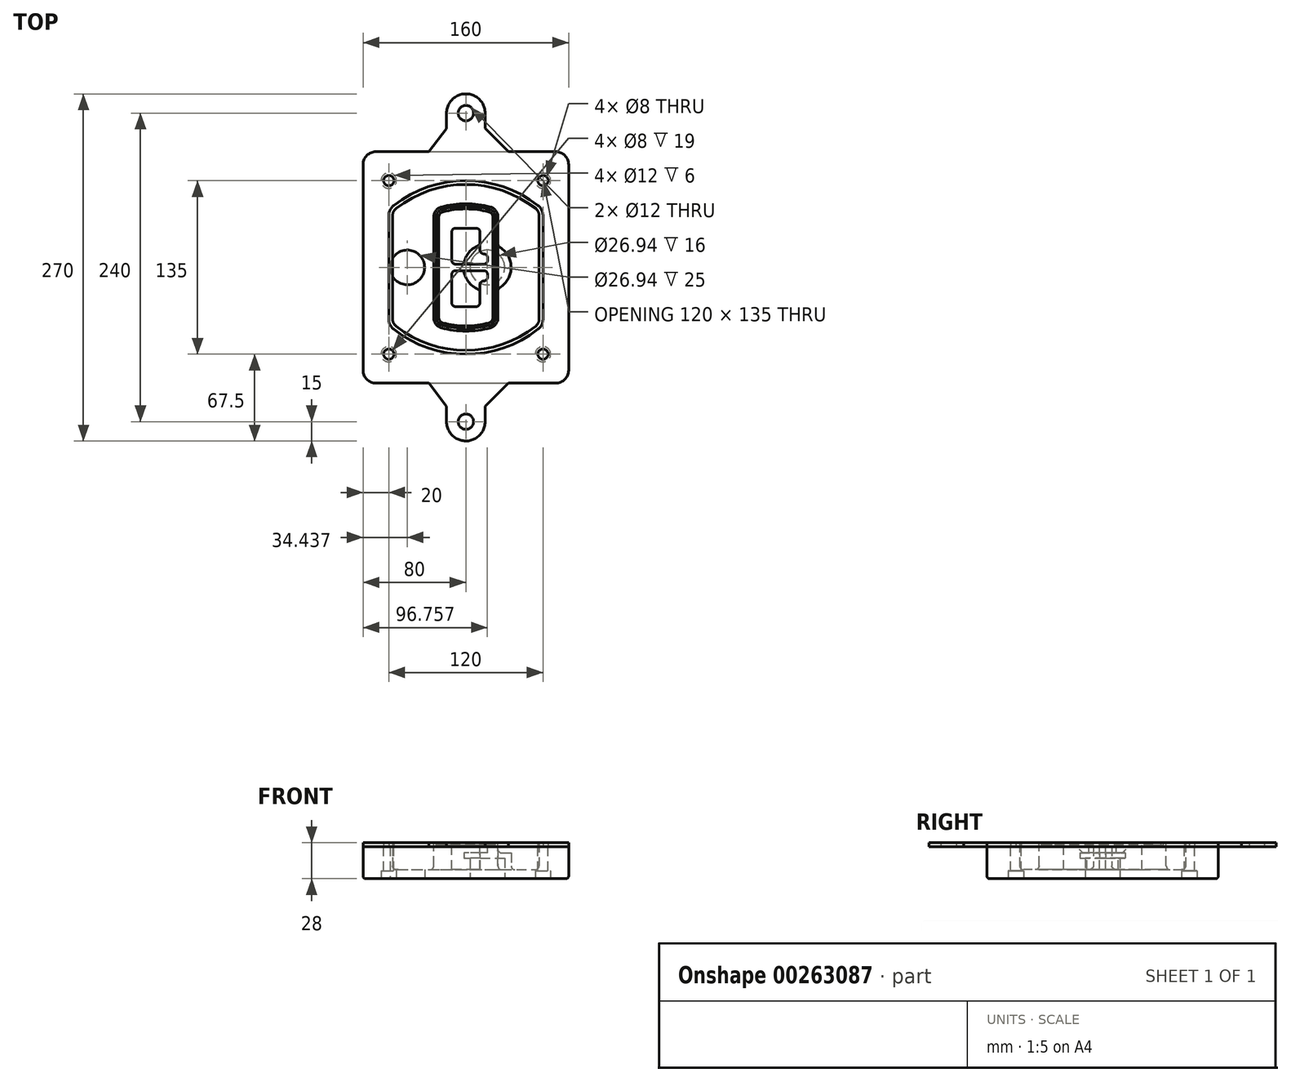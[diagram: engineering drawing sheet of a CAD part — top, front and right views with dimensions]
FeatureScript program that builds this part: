
annotation { "Feature Type Name" : "Feature", "Feature Type Description" : "" }
export const myFeature = defineFeature(function(context is Context, id is Id, definition is map)
    precondition{}
    {
        {
            var Q0;
            Q0=qCreatedBy(makeId("Top.planeOp"),FACE);
            var sketch = newSketch(context, id + "F0", { "sketchPlane" : qUnion([Q0])});
            skPoint(sketch, "E0.rect.middle", {"position": v(0, 0) * mm});
            skLineSegment(sketch, "E1.bottom", {"start": v(-70, -90) * mm, "end": v(70, -90) * mm});
            skLineSegment(sketch, "E1.top", {"start": v(-70, 90) * mm, "end": v(70, 90) * mm});
            skLineSegment(sketch, "E1.left", {"start": v(-80, -80) * mm, "end": v(-80, 80) * mm});
            skLineSegment(sketch, "E1.right", {"start": v(80, -80) * mm, "end": v(80, 80) * mm});
            skLineSegment(sketch, "E2", {"start": v(-80, 90) * mm, "end": v(80, -90) * mm, "construction": true});
            skLineSegment(sketch, "E3", {"start": v(80, 90) * mm, "end": v(-80, -90) * mm, "construction": true});
            skCircle(sketch, "E4", {"center": v(-60, 67.5) * mm, "radius": 4 * mm});
            skCircle(sketch, "E5", {"center": v(60, 67.5) * mm, "radius": 4 * mm});
            skCircle(sketch, "E6", {"center": v(60, -67.5) * mm, "radius": 4 * mm});
            skCircle(sketch, "E7", {"center": v(-60, -67.5) * mm, "radius": 4 * mm});
            skLineSegment(sketch, "E8", {"start": v(-60, 67.5) * mm, "end": v(60, 67.5) * mm, "construction": true});
            skLineSegment(sketch, "E9", {"start": v(60, 67.5) * mm, "end": v(60, -67.5) * mm, "construction": true});
            skLineSegment(sketch, "E10", {"start": v(60, -67.5) * mm, "end": v(-60, -67.5) * mm, "construction": true});
            skLineSegment(sketch, "E11", {"start": v(-60, -67.5) * mm, "end": v(-60, 67.5) * mm, "construction": true});
            skLineSegment(sketch, "E12", {"start": v(-60, 40.3) * mm, "end": v(-60, -40.3) * mm});
            skLineSegment(sketch, "E13", {"start": v(60, 40.3) * mm, "end": v(60, -40.3) * mm});
            skArc(sketch, "E14", {"start": v(56.15, 48.18) * mm, "mid": v(0, 67.5) * mm, "end": v(-56.15, 48.18) * mm});
            skArc(sketch, "E15", {"start": v(-56.15, -48.18) * mm, "mid": v(0, -67.5) * mm, "end": v(56.15, -48.18) * mm});
            skLineSegment(sketch, "E16", {"start": v(-60, 0) * mm, "end": v(60, 0) * mm, "construction": true});
            skPoint(sketch, "E17.visualSharp", {"position": v(-60, -45) * mm});
            skArc(sketch, "E17.filletArc", {"start": v(-60, -40.3) * mm, "mid": v(-58.99, -44.68) * mm, "end": v(-56.15, -48.18) * mm});
            skPoint(sketch, "E18.visualSharp", {"position": v(-60, 45) * mm});
            skArc(sketch, "E18.filletArc", {"start": v(-56.15, 48.18) * mm, "mid": v(-58.99, 44.68) * mm, "end": v(-60, 40.3) * mm});
            skPoint(sketch, "E19.visualSharp", {"position": v(60, 45) * mm});
            skArc(sketch, "E19.filletArc", {"start": v(60, 40.3) * mm, "mid": v(58.99, 44.68) * mm, "end": v(56.15, 48.18) * mm});
            skPoint(sketch, "E20.visualSharp", {"position": v(60, -45) * mm});
            skArc(sketch, "E20.filletArc", {"start": v(56.15, -48.18) * mm, "mid": v(58.99, -44.68) * mm, "end": v(60, -40.3) * mm});
            skPoint(sketch, "E21.visualSharp", {"position": v(-80, 90) * mm});
            skArc(sketch, "E21.filletArc", {"start": v(-70, 90) * mm, "mid": v(-77.07, 87.07) * mm, "end": v(-80, 80) * mm});
            skPoint(sketch, "E22.visualSharp", {"position": v(80, 90) * mm});
            skArc(sketch, "E22.filletArc", {"start": v(80, 80) * mm, "mid": v(77.07, 87.07) * mm, "end": v(70, 90) * mm});
            skPoint(sketch, "E23.visualSharp", {"position": v(80, -90) * mm});
            skArc(sketch, "E23.filletArc", {"start": v(70, -90) * mm, "mid": v(77.07, -87.07) * mm, "end": v(80, -80) * mm});
            skPoint(sketch, "E24.visualSharp", {"position": v(-80, -90) * mm});
            skArc(sketch, "E24.filletArc", {"start": v(-80, -80) * mm, "mid": v(-77.07, -87.07) * mm, "end": v(-70, -90) * mm});
            skArc(sketch, "E25.0", {"start": v(57, 40.3) * mm, "mid": v(56.3, 43.36) * mm, "end": v(54.3, 45.81) * mm});
            skLineSegment(sketch, "E25.1", {"start": v(57, 40.3) * mm, "end": v(57, -40.3) * mm});
            skArc(sketch, "E25.2", {"start": v(54.3, -45.81) * mm, "mid": v(56.3, -43.36) * mm, "end": v(57, -40.3) * mm});
            skArc(sketch, "E25.3", {"start": v(-54.3, -45.81) * mm, "mid": v(0, -64.5) * mm, "end": v(54.3, -45.81) * mm});
            skArc(sketch, "E25.4", {"start": v(-57, -40.3) * mm, "mid": v(-56.3, -43.36) * mm, "end": v(-54.3, -45.81) * mm});
            skArc(sketch, "E25.5", {"start": v(54.3, 45.81) * mm, "mid": v(0, 64.5) * mm, "end": v(-54.3, 45.81) * mm});
            skLineSegment(sketch, "E25.6", {"start": v(-57, 40.3) * mm, "end": v(-57, -40.3) * mm});
            skArc(sketch, "E25.7", {"start": v(-54.3, 45.81) * mm, "mid": v(-56.3, 43.36) * mm, "end": v(-57, 40.3) * mm});
            skArc(sketch, "E26.0", {"start": v(-58.62, 51.33) * mm, "mid": v(-62.58, 46.43) * mm, "end": v(-64, 40.3) * mm});
            skArc(sketch, "E26.1", {"start": v(58.62, 51.33) * mm, "mid": v(0, 71.5) * mm, "end": v(-58.62, 51.33) * mm});
            skArc(sketch, "E26.2", {"start": v(64, 40.3) * mm, "mid": v(62.58, 46.43) * mm, "end": v(58.62, 51.33) * mm});
            skLineSegment(sketch, "E26.3", {"start": v(64, 40.3) * mm, "end": v(64, -40.3) * mm});
            skArc(sketch, "E26.4", {"start": v(58.62, -51.33) * mm, "mid": v(62.58, -46.43) * mm, "end": v(64, -40.3) * mm});
            skLineSegment(sketch, "E26.5", {"start": v(-64, 40.3) * mm, "end": v(-64, -40.3) * mm});
            skArc(sketch, "E26.6", {"start": v(-58.62, -51.33) * mm, "mid": v(0, -71.5) * mm, "end": v(58.62, -51.33) * mm});
            skArc(sketch, "E26.7", {"start": v(-64, -40.3) * mm, "mid": v(-62.58, -46.43) * mm, "end": v(-58.62, -51.33) * mm});
            skSolve(sketch);
        }
        {
            var Q0;
            Q0=makeQuery(id+"F0.imprint","IMPRINT",FACE,{"disambiguationData":[TD([[makeQuery(id+"F0.imprint","IMPRINT",EDGE,{"derivedFrom":sQuery(id+"F0.wireOp",EDGE,"E1.bottom")}),1.0]])]});
            var Q1;
            Q1=makeQuery(id+"F0.imprint","IMPRINT",FACE,{"disambiguationData":[TD([[makeQuery(id+"F0.imprint","IMPRINT",EDGE,{"derivedFrom":sQuery(id+"F0.wireOp",EDGE,"E12")}),1.0]])]});
            var Q2;
            Q2=makeQuery(id+"F0.imprint","IMPRINT",FACE,{"disambiguationData":[TD([[makeQuery(id+"F0.imprint","IMPRINT",EDGE,{"derivedFrom":sQuery(id+"F0.wireOp",EDGE,"E25.0")}),1.0]])]});
            var Q3;
            Q3=makeQuery(id+"F0.imprint","IMPRINT",FACE,{"disambiguationData":[TD([[makeQuery(id+"F0.imprint","IMPRINT",EDGE,{"derivedFrom":sQuery(id+"F0.wireOp",EDGE,"E12")}),-1.0]])]});
            extrude(context, id + "F1", {"entities" : qUnion([Q0, Q1, Q2, Q3]), "oppositeDirection" : true, "depth" : 25 * mm});
        }
        {
            var Q0;
            Q0=makeQuery(id+"F0.imprint","IMPRINT",FACE,{"disambiguationData":[TD([[makeQuery(id+"F0.imprint","IMPRINT",EDGE,{"derivedFrom":sQuery(id+"F0.wireOp",EDGE,"E12")}),1.0]])]});
            extrude(context, id + "F2", {"entities" : qUnion([Q0]), "operationType" : NewBodyOperationType.ADD, "depth" : 3 * mm});
        }
        {
            var Q0;
            Q0=makeQuery(id+"F0.imprint","IMPRINT",FACE,{"disambiguationData":[TD([[makeQuery(id+"F0.imprint","IMPRINT",EDGE,{"derivedFrom":sQuery(id+"F0.wireOp",EDGE,"E25.0")}),1.0]])]});
            extrude(context, id + "F3", {"entities" : qUnion([Q0]), "operationType" : NewBodyOperationType.REMOVE, "oppositeDirection" : true, "depth" : 18 * mm});
        }
        {
            var Q0;
            Q0=makeQuery(id+"F2.opExtrude","CAP_FACE",FACE,{"disambiguationData":[OSD([sQuery(id+"F0.wireOp",EDGE,"E12"),sQuery(id+"F0.wireOp",EDGE,"E13"),sQuery(id+"F0.wireOp",EDGE,"E14"),sQuery(id+"F0.wireOp",EDGE,"E15"),sQuery(id+"F0.wireOp",EDGE,"E17.filletArc"),sQuery(id+"F0.wireOp",EDGE,"E18.filletArc"),sQuery(id+"F0.wireOp",EDGE,"E19.filletArc"),sQuery(id+"F0.wireOp",EDGE,"E20.filletArc"),sQuery(id+"F0.wireOp",EDGE,"E25.0"),sQuery(id+"F0.wireOp",EDGE,"E25.1"),sQuery(id+"F0.wireOp",EDGE,"E25.2"),sQuery(id+"F0.wireOp",EDGE,"E25.3"),sQuery(id+"F0.wireOp",EDGE,"E25.4"),sQuery(id+"F0.wireOp",EDGE,"E25.5"),sQuery(id+"F0.wireOp",EDGE,"E25.6"),sQuery(id+"F0.wireOp",EDGE,"E25.7")])],"isStart":false});
            var sketch = newSketch(context, id + "F4", { "sketchPlane" : qUnion([Q0])});
            skArc(sketch, "E27.0", {"start": v(-19.08, -46.97) * mm, "mid": v(0, -49.5) * mm, "end": v(19.08, -46.97) * mm});
            skArc(sketch, "E28.0", {"start": v(19.08, 46.97) * mm, "mid": v(0, 49.5) * mm, "end": v(-19.08, 46.97) * mm});
            skLineSegment(sketch, "E29", {"start": v(-25, 39.25) * mm, "end": v(-25, -39.25) * mm});
            skLineSegment(sketch, "E30", {"start": v(25, 39.25) * mm, "end": v(25, -39.25) * mm});
            skLineSegment(sketch, "E31", {"start": v(-25, 45.1) * mm, "end": v(25, 45.1) * mm, "construction": true});
            skLineSegment(sketch, "E32", {"start": v(-25, -45.1) * mm, "end": v(25, -45.1) * mm, "construction": true});
            skPoint(sketch, "E33.visualSharp", {"position": v(-25, 45.1) * mm});
            skArc(sketch, "E33.filletArc", {"start": v(-19.08, 46.97) * mm, "mid": v(-23.35, 44.11) * mm, "end": v(-25, 39.25) * mm});
            skPoint(sketch, "E34.visualSharp", {"position": v(25, 45.1) * mm});
            skArc(sketch, "E34.filletArc", {"start": v(25, 39.25) * mm, "mid": v(23.35, 44.11) * mm, "end": v(19.08, 46.97) * mm});
            skPoint(sketch, "E35.visualSharp", {"position": v(25, -45.1) * mm});
            skArc(sketch, "E35.filletArc", {"start": v(19.08, -46.97) * mm, "mid": v(23.35, -44.11) * mm, "end": v(25, -39.25) * mm});
            skPoint(sketch, "E36.visualSharp", {"position": v(-25, -45.1) * mm});
            skArc(sketch, "E36.filletArc", {"start": v(-25, -39.25) * mm, "mid": v(-23.35, -44.11) * mm, "end": v(-19.08, -46.97) * mm});
            skArc(sketch, "E37.0", {"start": v(54.3, 45.81) * mm, "mid": v(0, 64.5) * mm, "end": v(-54.3, 45.81) * mm});
            skArc(sketch, "E37.1", {"start": v(-54.3, 45.81) * mm, "mid": v(-56.3, 43.36) * mm, "end": v(-57, 40.3) * mm});
            skLineSegment(sketch, "E37.2", {"start": v(-57, 40.3) * mm, "end": v(-57, -40.3) * mm});
            skArc(sketch, "E37.3", {"start": v(-57, -40.3) * mm, "mid": v(-56.3, -43.36) * mm, "end": v(-54.3, -45.81) * mm});
            skArc(sketch, "E37.4", {"start": v(-54.3, -45.81) * mm, "mid": v(0, -64.5) * mm, "end": v(54.3, -45.81) * mm});
            skArc(sketch, "E37.5", {"start": v(54.3, -45.81) * mm, "mid": v(56.3, -43.36) * mm, "end": v(57, -40.3) * mm});
            skLineSegment(sketch, "E37.6", {"start": v(57, 40.3) * mm, "end": v(57, -40.3) * mm});
            skArc(sketch, "E37.7", {"start": v(57, 40.3) * mm, "mid": v(56.3, 43.36) * mm, "end": v(54.3, 45.81) * mm});
            skLineSegment(sketch, "E38.0", {"start": v(23, 39.25) * mm, "end": v(23, -39.25) * mm});
            skArc(sketch, "E38.1", {"start": v(18.56, -45.04) * mm, "mid": v(21.76, -42.9) * mm, "end": v(23, -39.25) * mm});
            skArc(sketch, "E38.2", {"start": v(-18.56, -45.04) * mm, "mid": v(0, -47.5) * mm, "end": v(18.56, -45.04) * mm});
            skArc(sketch, "E38.3", {"start": v(-23, -39.25) * mm, "mid": v(-21.76, -42.9) * mm, "end": v(-18.56, -45.04) * mm});
            skLineSegment(sketch, "E38.4", {"start": v(-23, 39.25) * mm, "end": v(-23, -39.25) * mm});
            skArc(sketch, "E38.5", {"start": v(23, 39.25) * mm, "mid": v(21.76, 42.9) * mm, "end": v(18.56, 45.04) * mm});
            skArc(sketch, "E38.6", {"start": v(-18.56, 45.04) * mm, "mid": v(-21.76, 42.9) * mm, "end": v(-23, 39.25) * mm});
            skArc(sketch, "E38.7", {"start": v(18.56, 45.04) * mm, "mid": v(0, 47.5) * mm, "end": v(-18.56, 45.04) * mm});
            skArc(sketch, "E39.0", {"start": v(21, 39.25) * mm, "mid": v(20.18, 41.68) * mm, "end": v(18.04, 43.1) * mm});
            skLineSegment(sketch, "E39.1", {"start": v(21, 39.25) * mm, "end": v(21, -39.25) * mm});
            skArc(sketch, "E39.2", {"start": v(18.04, -43.1) * mm, "mid": v(20.18, -41.68) * mm, "end": v(21, -39.25) * mm});
            skArc(sketch, "E39.3", {"start": v(-18.04, -43.1) * mm, "mid": v(0, -45.5) * mm, "end": v(18.04, -43.1) * mm});
            skArc(sketch, "E39.4", {"start": v(-21, -39.25) * mm, "mid": v(-20.18, -41.68) * mm, "end": v(-18.04, -43.1) * mm});
            skArc(sketch, "E39.5", {"start": v(18.04, 43.1) * mm, "mid": v(0, 45.5) * mm, "end": v(-18.04, 43.1) * mm});
            skLineSegment(sketch, "E39.6", {"start": v(-21, 39.25) * mm, "end": v(-21, -39.25) * mm});
            skArc(sketch, "E39.7", {"start": v(-18.04, 43.1) * mm, "mid": v(-20.18, 41.68) * mm, "end": v(-21, 39.25) * mm});
            skLineSegment(sketch, "E40", {"start": v(-25, 0) * mm, "end": v(25, 0) * mm, "construction": true});
            skLineSegment(sketch, "E41", {"start": v(-11, 5.5) * mm, "end": v(-11, 27.5) * mm});
            skLineSegment(sketch, "E42", {"start": v(-8, 30.5) * mm, "end": v(8, 30.5) * mm});
            skLineSegment(sketch, "E43", {"start": v(11, 27.5) * mm, "end": v(11, 13.5) * mm});
            skLineSegment(sketch, "E44", {"start": v(14, 10.5) * mm, "end": v(14, 10.5) * mm});
            skLineSegment(sketch, "E45", {"start": v(17, 7.5) * mm, "end": v(17, 5.5) * mm});
            skLineSegment(sketch, "E46", {"start": v(14, 2.5) * mm, "end": v(-8, 2.5) * mm});
            skPoint(sketch, "E47.visualSharp", {"position": v(-11, 30.5) * mm});
            skArc(sketch, "E47.filletArc", {"start": v(-8, 30.5) * mm, "mid": v(-10.12, 29.62) * mm, "end": v(-11, 27.5) * mm});
            skPoint(sketch, "E48.visualSharp", {"position": v(11, 30.5) * mm});
            skArc(sketch, "E48.filletArc", {"start": v(11, 27.5) * mm, "mid": v(10.12, 29.62) * mm, "end": v(8, 30.5) * mm});
            skPoint(sketch, "E49.visualSharp", {"position": v(11, 10.5) * mm});
            skArc(sketch, "E49.filletArc", {"start": v(11, 13.5) * mm, "mid": v(11.88, 11.38) * mm, "end": v(14, 10.5) * mm});
            skPoint(sketch, "E50.visualSharp", {"position": v(17, 10.5) * mm});
            skArc(sketch, "E50.filletArc", {"start": v(17, 7.5) * mm, "mid": v(16.12, 9.62) * mm, "end": v(14, 10.5) * mm});
            skPoint(sketch, "E51.visualSharp", {"position": v(17, 2.5) * mm});
            skArc(sketch, "E51.filletArc", {"start": v(14, 2.5) * mm, "mid": v(16.12, 3.38) * mm, "end": v(17, 5.5) * mm});
            skPoint(sketch, "E52.visualSharp", {"position": v(-11, 2.5) * mm});
            skArc(sketch, "E52.filletArc", {"start": v(-11, 5.5) * mm, "mid": v(-10.12, 3.38) * mm, "end": v(-8, 2.5) * mm});
            skLineSegment(sketch, "E53.0.MirrorCS", {"start": v(14, -2.5) * mm, "end": v(-8, -2.5) * mm});
            skArc(sketch, "E54.0.MirrorCS", {"start": v(-11, -5.5) * mm, "mid": v(-10.12, -3.38) * mm, "end": v(-8, -2.5) * mm});
            skLineSegment(sketch, "E55.0.MirrorCS", {"start": v(-11, -5.5) * mm, "end": v(-11, -27.5) * mm});
            skArc(sketch, "E56.0.MirrorCS", {"start": v(-8, -30.5) * mm, "mid": v(-10.12, -29.62) * mm, "end": v(-11, -27.5) * mm});
            skLineSegment(sketch, "E57.0.MirrorCS", {"start": v(-8, -30.5) * mm, "end": v(8, -30.5) * mm});
            skArc(sketch, "E58.0.MirrorCS", {"start": v(11, -27.5) * mm, "mid": v(10.12, -29.62) * mm, "end": v(8, -30.5) * mm});
            skLineSegment(sketch, "E59.0.MirrorCS", {"start": v(11, -27.5) * mm, "end": v(11, -13.5) * mm});
            skArc(sketch, "E60.0.MirrorCS", {"start": v(11, -13.5) * mm, "mid": v(11.88, -11.38) * mm, "end": v(14, -10.5) * mm});
            skArc(sketch, "E61.0.MirrorCS", {"start": v(17, -7.5) * mm, "mid": v(16.12, -9.62) * mm, "end": v(14, -10.5) * mm});
            skLineSegment(sketch, "E62.0.MirrorCS", {"start": v(17, -7.5) * mm, "end": v(17, -5.5) * mm});
            skArc(sketch, "E63.0.MirrorCS", {"start": v(14, -2.5) * mm, "mid": v(16.12, -3.38) * mm, "end": v(17, -5.5) * mm});
            skSolve(sketch);
        }
        {
            var Q0;
            Q0=makeQuery(id+"F4.imprint","IMPRINT",FACE,{"disambiguationData":[TD([[makeQuery(id+"F4.imprint","IMPRINT",EDGE,{"derivedFrom":sQuery(id+"F4.wireOp",EDGE,"E27.0")}),1.0]])]});
            var Q1;
            Q1=makeQuery(id+"F4.imprint","IMPRINT",FACE,{"disambiguationData":[TD([[makeQuery(id+"F4.imprint","IMPRINT",EDGE,{"derivedFrom":sQuery(id+"F4.wireOp",EDGE,"E38.0")}),-1.0]])]});
            var Q2;
            Q2=makeQuery(id+"F4.imprint","IMPRINT",FACE,{"disambiguationData":[TD([[makeQuery(id+"F4.imprint","IMPRINT",EDGE,{"derivedFrom":sQuery(id+"F4.wireOp",EDGE,"E39.0")}),1.0]])]});
            extrude(context, id + "F5", {"entities" : qUnion([Q0, Q1, Q2]), "operationType" : NewBodyOperationType.ADD, "endBound" : BoundingType.UP_TO_NEXT, "oppositeDirection" : true, "depth" : 25 * mm});
        }
        {
            var Q0;
            Q0=makeQuery(id+"F4.imprint","IMPRINT",FACE,{"disambiguationData":[TD([[makeQuery(id+"F4.imprint","IMPRINT",EDGE,{"derivedFrom":sQuery(id+"F4.wireOp",EDGE,"E38.0")}),-1.0]])]});
            extrude(context, id + "F6", {"entities" : qUnion([Q0]), "operationType" : NewBodyOperationType.REMOVE, "oppositeDirection" : true, "depth" : 2 * mm});
        }
        {
            var Q0;
            Q0=makeQuery(id+"F1.opExtrude","CAP_FACE",FACE,{"disambiguationData":[OSD([sQuery(id+"F0.wireOp",EDGE,"E1.bottom"),sQuery(id+"F0.wireOp",EDGE,"E1.top"),sQuery(id+"F0.wireOp",EDGE,"E1.left"),sQuery(id+"F0.wireOp",EDGE,"E1.right"),sQuery(id+"F0.wireOp",EDGE,"E4"),sQuery(id+"F0.wireOp",EDGE,"E5"),sQuery(id+"F0.wireOp",EDGE,"E6"),sQuery(id+"F0.wireOp",EDGE,"E7"),sQuery(id+"F0.wireOp",EDGE,"E21.filletArc"),sQuery(id+"F0.wireOp",EDGE,"E22.filletArc"),sQuery(id+"F0.wireOp",EDGE,"E23.filletArc"),sQuery(id+"F0.wireOp",EDGE,"E24.filletArc")])],"isStart":false});
            var sketch = newSketch(context, id + "F7", { "sketchPlane" : qUnion([Q0])});
            skCircle(sketch, "E64", {"center": v(16.76, 0) * mm, "radius": 13.47 * mm});
            skCircle(sketch, "E65", {"center": v(-45.56, 0) * mm, "radius": 13.47 * mm});
            skLineSegment(sketch, "E66", {"start": v(80, 0) * mm, "end": v(-80, 0) * mm});
            skCircle(sketch, "E67", {"center": v(16.76, 0) * mm, "radius": 18.47 * mm});
            skCircle(sketch, "E68", {"center": v(60, -67.5) * mm, "radius": 6 * mm});
            skCircle(sketch, "E69", {"center": v(-60, -67.5) * mm, "radius": 6 * mm});
            skCircle(sketch, "E70", {"center": v(-60, 67.5) * mm, "radius": 6 * mm});
            skCircle(sketch, "E71", {"center": v(60, 67.5) * mm, "radius": 6 * mm});
            skSolve(sketch);
        }
        {
            var Q0;
            {var subQ1=sQuery(id+"F7.wireOp",EDGE,"E66");var subQ4=sQuery(id+"F7.wireOp",EDGE,"E64");var subQ6=makeQuery(id+"F7.imprint","INTERSECT",VERTEX,{"disambiguationData":[OD(0.0)],"derivedFrom":[subQ4,subQ1]});Q0=makeQuery(id+"F7.imprint","IMPRINT",FACE,{"disambiguationData":[TD([[makeQuery(id+"F7.imprint","IMPRINT",EDGE,{"disambiguationData":[TD([[subQ6,-1.0]])],"derivedFrom":subQ4}),-1.0]])]});}
            var Q1;
            {var subQ0=sQuery(id+"F7.wireOp",EDGE,"E66");var subQ1=sQuery(id+"F7.wireOp",EDGE,"E64");var subQ3=makeQuery(id+"F7.imprint","INTERSECT",VERTEX,{"disambiguationData":[OD(0.0)],"derivedFrom":[subQ1,subQ0]});Q1=makeQuery(id+"F7.imprint","IMPRINT",FACE,{"disambiguationData":[TD([[makeQuery(id+"F7.imprint","IMPRINT",EDGE,{"disambiguationData":[TD([[subQ3,-1.0]])],"derivedFrom":subQ1}),1.0]])]});}
            var Q2;
            {var subQ0=sQuery(id+"F7.wireOp",EDGE,"E66");var subQ1=sQuery(id+"F7.wireOp",EDGE,"E64");var subQ3=makeQuery(id+"F7.imprint","INTERSECT",VERTEX,{"disambiguationData":[OD(0.0)],"derivedFrom":[subQ1,subQ0]});Q2=makeQuery(id+"F7.imprint","IMPRINT",FACE,{"disambiguationData":[TD([[makeQuery(id+"F7.imprint","IMPRINT",EDGE,{"disambiguationData":[TD([[subQ3,1.0]])],"derivedFrom":subQ1}),1.0]])]});}
            var Q3;
            {var subQ1=sQuery(id+"F7.wireOp",EDGE,"E66");var subQ4=sQuery(id+"F7.wireOp",EDGE,"E64");var subQ6=makeQuery(id+"F7.imprint","INTERSECT",VERTEX,{"disambiguationData":[OD(0.0)],"derivedFrom":[subQ4,subQ1]});Q3=makeQuery(id+"F7.imprint","IMPRINT",FACE,{"disambiguationData":[TD([[makeQuery(id+"F7.imprint","IMPRINT",EDGE,{"disambiguationData":[TD([[subQ6,1.0]])],"derivedFrom":subQ4}),-1.0]])]});}
            extrude(context, id + "F8", {"entities" : qUnion([Q0, Q1, Q2, Q3]), "operationType" : NewBodyOperationType.ADD, "oppositeDirection" : true, "depth" : 20 * mm});
        }
        {
            var Q0;
            {var subQ0=sQuery(id+"F7.wireOp",EDGE,"E66");var subQ1=sQuery(id+"F7.wireOp",EDGE,"E64");var subQ3=makeQuery(id+"F7.imprint","INTERSECT",VERTEX,{"disambiguationData":[OD(0.0)],"derivedFrom":[subQ1,subQ0]});Q0=makeQuery(id+"F7.imprint","IMPRINT",FACE,{"disambiguationData":[TD([[makeQuery(id+"F7.imprint","IMPRINT",EDGE,{"disambiguationData":[TD([[subQ3,-1.0]])],"derivedFrom":subQ1}),1.0]])]});}
            var Q1;
            {var subQ0=sQuery(id+"F7.wireOp",EDGE,"E66");var subQ1=sQuery(id+"F7.wireOp",EDGE,"E64");var subQ3=makeQuery(id+"F7.imprint","INTERSECT",VERTEX,{"disambiguationData":[OD(0.0)],"derivedFrom":[subQ1,subQ0]});Q1=makeQuery(id+"F7.imprint","IMPRINT",FACE,{"disambiguationData":[TD([[makeQuery(id+"F7.imprint","IMPRINT",EDGE,{"disambiguationData":[TD([[subQ3,1.0]])],"derivedFrom":subQ1}),1.0]])]});}
            extrude(context, id + "F9", {"entities" : qUnion([Q0, Q1]), "operationType" : NewBodyOperationType.REMOVE, "oppositeDirection" : true, "depth" : 16 * mm});
        }
        {
            var Q0;
            {var subQ0=sQuery(id+"F7.wireOp",EDGE,"E66");var subQ1=sQuery(id+"F7.wireOp",EDGE,"E65");var subQ3=makeQuery(id+"F7.imprint","INTERSECT",VERTEX,{"disambiguationData":[OD(0.0)],"derivedFrom":[subQ1,subQ0]});Q0=makeQuery(id+"F7.imprint","IMPRINT",FACE,{"disambiguationData":[TD([[makeQuery(id+"F7.imprint","IMPRINT",EDGE,{"disambiguationData":[TD([[subQ3,-1.0]])],"derivedFrom":subQ1}),1.0]])]});}
            var Q1;
            {var subQ0=sQuery(id+"F7.wireOp",EDGE,"E66");var subQ1=sQuery(id+"F7.wireOp",EDGE,"E65");var subQ3=makeQuery(id+"F7.imprint","INTERSECT",VERTEX,{"disambiguationData":[OD(0.0)],"derivedFrom":[subQ1,subQ0]});Q1=makeQuery(id+"F7.imprint","IMPRINT",FACE,{"disambiguationData":[TD([[makeQuery(id+"F7.imprint","IMPRINT",EDGE,{"disambiguationData":[TD([[subQ3,1.0]])],"derivedFrom":subQ1}),1.0]])]});}
            extrude(context, id + "F10", {"entities" : qUnion([Q0, Q1]), "operationType" : NewBodyOperationType.REMOVE, "oppositeDirection" : true, "depth" : 25 * mm});
        }
        {
            var Q0;
            Q0=makeQuery(id+"F7.imprint","IMPRINT",FACE,{"disambiguationData":[TD([[makeQuery(id+"F7.imprint","IMPRINT",EDGE,{"derivedFrom":sQuery(id+"F7.wireOp",EDGE,"E68")}),1.0]])]});
            var Q1;
            Q1=makeQuery(id+"F7.imprint","IMPRINT",FACE,{"disambiguationData":[TD([[makeQuery(id+"F7.imprint","IMPRINT",EDGE,{"derivedFrom":makeQuery(id+"F1.opExtrude","CAP_EDGE",EDGE,{"disambiguationData":[OSD([sQuery(id+"F0.wireOp",EDGE,"E5")])],"isStart":false})}),-1.0]])]});
            var Q2;
            Q2=makeQuery(id+"F7.imprint","IMPRINT",FACE,{"disambiguationData":[TD([[makeQuery(id+"F7.imprint","IMPRINT",EDGE,{"derivedFrom":sQuery(id+"F7.wireOp",EDGE,"E69")}),1.0]])]});
            var Q3;
            Q3=makeQuery(id+"F7.imprint","IMPRINT",FACE,{"disambiguationData":[TD([[makeQuery(id+"F7.imprint","IMPRINT",EDGE,{"derivedFrom":makeQuery(id+"F1.opExtrude","CAP_EDGE",EDGE,{"disambiguationData":[OSD([sQuery(id+"F0.wireOp",EDGE,"E4")])],"isStart":false})}),-1.0]])]});
            var Q4;
            Q4=makeQuery(id+"F7.imprint","IMPRINT",FACE,{"disambiguationData":[TD([[makeQuery(id+"F7.imprint","IMPRINT",EDGE,{"derivedFrom":sQuery(id+"F7.wireOp",EDGE,"E70")}),1.0]])]});
            var Q5;
            Q5=makeQuery(id+"F7.imprint","IMPRINT",FACE,{"disambiguationData":[TD([[makeQuery(id+"F7.imprint","IMPRINT",EDGE,{"derivedFrom":makeQuery(id+"F1.opExtrude","CAP_EDGE",EDGE,{"disambiguationData":[OSD([sQuery(id+"F0.wireOp",EDGE,"E7")])],"isStart":false})}),-1.0]])]});
            var Q6;
            Q6=makeQuery(id+"F7.imprint","IMPRINT",FACE,{"disambiguationData":[TD([[makeQuery(id+"F7.imprint","IMPRINT",EDGE,{"derivedFrom":sQuery(id+"F7.wireOp",EDGE,"E71")}),1.0]])]});
            var Q7;
            Q7=makeQuery(id+"F7.imprint","IMPRINT",FACE,{"disambiguationData":[TD([[makeQuery(id+"F7.imprint","IMPRINT",EDGE,{"derivedFrom":makeQuery(id+"F1.opExtrude","CAP_EDGE",EDGE,{"disambiguationData":[OSD([sQuery(id+"F0.wireOp",EDGE,"E6")])],"isStart":false})}),-1.0]])]});
            extrude(context, id + "F11", {"entities" : qUnion([Q0, Q1, Q2, Q3, Q4, Q5, Q6, Q7]), "operationType" : NewBodyOperationType.REMOVE, "oppositeDirection" : true, "depth" : 6 * mm});
        }
        {
            var Q0;
            Q0=makeQuery(id+"F9.boolean.opBoolean","COPY",FACE,{"derivedFrom":makeQuery(id+"F9.opExtrude","CAP_FACE",FACE,{"disambiguationData":[OSD([sQuery(id+"F7.wireOp",EDGE,"E64")])],"isStart":false})});
            var sketch = newSketch(context, id + "F12", { "sketchPlane" : qUnion([Q0])});
            skArc(sketch, "E72.0", {"start": v(11, 17.55) * mm, "mid": v(2.57, 11.82) * mm, "end": v(-1.54, 2.5) * mm});
            skArc(sketch, "E72.1", {"start": v(-1.54, -2.5) * mm, "mid": v(2.57, -11.82) * mm, "end": v(11, -17.55) * mm});
            skLineSegment(sketch, "E73", {"start": v(-1.54, -2.5) * mm, "end": v(14, -2.5) * mm});
            skLineSegment(sketch, "E74.0", {"start": v(14, 2.5) * mm, "end": v(-1.54, 2.5) * mm});
            skArc(sketch, "E74.1", {"start": v(14, 2.5) * mm, "mid": v(16.12, 3.38) * mm, "end": v(17, 5.5) * mm});
            skLineSegment(sketch, "E74.2", {"start": v(17, 7.5) * mm, "end": v(17, 5.5) * mm});
            skArc(sketch, "E74.3", {"start": v(17, 7.5) * mm, "mid": v(16.12, 9.62) * mm, "end": v(14, 10.5) * mm});
            skArc(sketch, "E74.4", {"start": v(11, 13.5) * mm, "mid": v(11.88, 11.38) * mm, "end": v(14, 10.5) * mm});
            skLineSegment(sketch, "E74.5", {"start": v(11, 17.55) * mm, "end": v(11, 13.5) * mm});
            skLineSegment(sketch, "E74.7", {"start": v(14, -2.5) * mm, "end": v(-1.54, -2.5) * mm});
            skArc(sketch, "E74.8", {"start": v(14, -2.5) * mm, "mid": v(16.12, -3.38) * mm, "end": v(17, -5.5) * mm});
            skLineSegment(sketch, "E74.9", {"start": v(17, -7.5) * mm, "end": v(17, -5.5) * mm});
            skArc(sketch, "E74.10", {"start": v(17, -7.5) * mm, "mid": v(16.12, -9.62) * mm, "end": v(14, -10.5) * mm});
            skArc(sketch, "E74.11", {"start": v(11, -13.5) * mm, "mid": v(11.88, -11.38) * mm, "end": v(14, -10.5) * mm});
            skLineSegment(sketch, "E74.12", {"start": v(11, -17.55) * mm, "end": v(11, -13.5) * mm});
            skPoint(sketch, "E75.orphan", {"position": v(11, -27.5) * mm});
            skPoint(sketch, "E76.orphan", {"position": v(-8, -2.5) * mm});
            skPoint(sketch, "E77.orphan", {"position": v(-8, 2.5) * mm});
            skPoint(sketch, "E78.orphan", {"position": v(11, 27.5) * mm});
            skSolve(sketch);
        }
        {
            var Q0;
            {var subQ7=sQuery(id+"F12.wireOp",EDGE,"E72.0");var subQ14=sQuery(id+"F12.wireOp",EDGE,"E72.1");var subQ16=sQuery(id+"F12.wireOp",EDGE,"E74.1");var subQ18=sQuery(id+"F12.wireOp",EDGE,"E74.8");Q0=qUnion([makeQuery(id+"F12.imprint","IMPRINT",FACE,{"disambiguationData":[TD([[makeQuery(id+"F12.imprint","IMPRINT",EDGE,{"derivedFrom":subQ7}),1.0]])]}),makeQuery(id+"F12.imprint","IMPRINT",FACE,{"disambiguationData":[TD([[makeQuery(id+"F12.imprint","IMPRINT",EDGE,{"derivedFrom":subQ14}),1.0]])]}),makeQuery(id+"F12.imprint","IMPRINT",FACE,{"disambiguationData":[TD([[makeQuery(id+"F12.imprint","IMPRINT",EDGE,{"derivedFrom":subQ16}),1.0]])]}),makeQuery(id+"F12.imprint","IMPRINT",FACE,{"disambiguationData":[TD([[makeQuery(id+"F12.imprint","IMPRINT",EDGE,{"derivedFrom":subQ18}),-1.0]])]})]);}
            var Q1;
            Q1=makeQuery(id+"F5.boolean.opBoolean","SPLIT",FACE,{"disambiguationData":[TD([makeQuery(id+"F5.opExtrude","SWEPT_FACE",FACE,{"disambiguationData":[OSD([sQuery(id+"F4.wireOp",EDGE,"E41")])]})])],"derivedFrom":makeQuery(id+"F3.boolean.opBoolean","COPY",FACE,{"derivedFrom":makeQuery(id+"F3.opExtrude","CAP_FACE",FACE,{"disambiguationData":[OSD([sQuery(id+"F0.wireOp",EDGE,"E25.0"),sQuery(id+"F0.wireOp",EDGE,"E25.1"),sQuery(id+"F0.wireOp",EDGE,"E25.2"),sQuery(id+"F0.wireOp",EDGE,"E25.3"),sQuery(id+"F0.wireOp",EDGE,"E25.4"),sQuery(id+"F0.wireOp",EDGE,"E25.5"),sQuery(id+"F0.wireOp",EDGE,"E25.6"),sQuery(id+"F0.wireOp",EDGE,"E25.7")])],"isStart":false})})});
            extrude(context, id + "F13", {"entities" : qUnion([Q0]), "operationType" : NewBodyOperationType.REMOVE, "endBound" : BoundingType.UP_TO_SURFACE, "endBoundEntityFace" : qUnion([Q1]), "depth" : 25 * mm});
        }
        {
            var Q0;
            Q0=makeQuery(id+"F3.boolean.opBoolean","COPY",EDGE,{"derivedFrom":makeQuery(id+"F3.opExtrude","CAP_EDGE",EDGE,{"disambiguationData":[OSD([sQuery(id+"F0.wireOp",EDGE,"E25.6")])],"isStart":false})});
            var Q1;
            Q1=makeQuery(id+"F8.boolean.opBoolean","INTERSECT",EDGE,{"derivedFrom":[makeQuery(id+"F5.opExtrude","SWEPT_FACE",FACE,{"disambiguationData":[OSD([sQuery(id+"F4.wireOp",EDGE,"E30")])]}),makeQuery(id+"F8.opExtrude","CAP_FACE",FACE,{"disambiguationData":[OSD([sQuery(id+"F7.wireOp",EDGE,"E67")])],"isStart":false})]});
            var Q2;
            Q2=makeQuery(id+"F8.boolean.opBoolean","INTERSECT",EDGE,{"disambiguationData":[OD(1.0)],"derivedFrom":[makeQuery(id+"F5.opExtrude","SWEPT_FACE",FACE,{"disambiguationData":[OSD([sQuery(id+"F4.wireOp",EDGE,"E30")])]}),makeQuery(id+"F8.opExtrude","SWEPT_FACE",FACE,{"disambiguationData":[OSD([sQuery(id+"F7.wireOp",EDGE,"E67")])]})]});
            var Q3;
            {var subQ0=sQuery(id+"F4.wireOp",EDGE,"E30");Q3=makeQuery(id+"F8.boolean.opBoolean","SPLIT",EDGE,{"disambiguationData":[TD([makeQuery(id+"F5.opExtrude","SWEPT_FACE",FACE,{"disambiguationData":[OSD([sQuery(id+"F4.wireOp",EDGE,"E35.filletArc")])]})])],"derivedFrom":makeQuery(id+"F5.opExtrude","CAP_EDGE",EDGE,{"disambiguationData":[OSD([subQ0])],"isStart":false})});}
            var Q4;
            {var subQ0=sQuery(id+"F0.wireOp",EDGE,"E25.7");var subQ1=sQuery(id+"F0.wireOp",EDGE,"E25.1");var subQ2=sQuery(id+"F0.wireOp",EDGE,"E25.6");var subQ3=sQuery(id+"F0.wireOp",EDGE,"E25.5");var subQ4=sQuery(id+"F0.wireOp",EDGE,"E25.4");var subQ5=sQuery(id+"F0.wireOp",EDGE,"E25.0");var subQ6=sQuery(id+"F0.wireOp",EDGE,"E25.2");var subQ7=sQuery(id+"F0.wireOp",EDGE,"E25.3");Q4=makeQuery(id+"F8.boolean.opBoolean","INTERSECT",EDGE,{"derivedFrom":[makeQuery(id+"F5.boolean.opBoolean","SPLIT",FACE,{"disambiguationData":[TD([makeQuery(id+"F2.opExtrude","SWEPT_FACE",FACE,{"disambiguationData":[OSD([subQ5])]})])],"derivedFrom":makeQuery(id+"F3.boolean.opBoolean","COPY",FACE,{"derivedFrom":makeQuery(id+"F3.opExtrude","CAP_FACE",FACE,{"disambiguationData":[OSD([subQ5,subQ1,subQ6,subQ7,subQ4,subQ3,subQ2,subQ0])],"isStart":false})})}),makeQuery(id+"F8.opExtrude","SWEPT_FACE",FACE,{"disambiguationData":[OSD([sQuery(id+"F7.wireOp",EDGE,"E67")])]})]});}
            var Q5;
            Q5=makeQuery(id+"F8.boolean.opBoolean","INTERSECT",EDGE,{"disambiguationData":[OD(0.0)],"derivedFrom":[makeQuery(id+"F5.opExtrude","SWEPT_FACE",FACE,{"disambiguationData":[OSD([sQuery(id+"F4.wireOp",EDGE,"E30")])]}),makeQuery(id+"F8.opExtrude","SWEPT_FACE",FACE,{"disambiguationData":[OSD([sQuery(id+"F7.wireOp",EDGE,"E67")])]})]});
            fillet(context, id + "F14", {"entities" : qUnion([Q0, Q1, Q2, Q3, Q4, Q5]), "radius" : 3 * mm, "tangentPropagation" : true, "allowEdgeOverflow" : false});
        }
        {
            var Q0;
            Q0=makeQuery(id+"F1.opExtrude","CAP_EDGE",EDGE,{"disambiguationData":[OSD([sQuery(id+"F0.wireOp",EDGE,"E1.bottom")])],"isStart":false});
            fillet(context, id + "F15", {"entities" : qUnion([Q0]), "radius" : 2 * mm, "tangentPropagation" : true, "allowEdgeOverflow" : false});
        }
        {
            var Q0;
            {var subQ0=sQuery(id+"F0.wireOp",EDGE,"E22.filletArc");var subQ1=sQuery(id+"F0.wireOp",EDGE,"E7");var subQ2=sQuery(id+"F0.wireOp",EDGE,"E6");var subQ3=sQuery(id+"F0.wireOp",EDGE,"E5");var subQ4=sQuery(id+"F0.wireOp",EDGE,"E4");var subQ5=sQuery(id+"F0.wireOp",EDGE,"E1.bottom");var subQ6=sQuery(id+"F0.wireOp",EDGE,"E21.filletArc");var subQ7=sQuery(id+"F0.wireOp",EDGE,"E1.top");var subQ8=sQuery(id+"F0.wireOp",EDGE,"E1.left");var subQ9=sQuery(id+"F0.wireOp",EDGE,"E1.right");var subQ10=sQuery(id+"F0.wireOp",EDGE,"E23.filletArc");var subQ11=sQuery(id+"F0.wireOp",EDGE,"E24.filletArc");Q0=makeQuery(id+"F2.boolean.opBoolean","SPLIT",FACE,{"disambiguationData":[TD([makeQuery(id+"F1.opExtrude","SWEPT_FACE",FACE,{"disambiguationData":[OSD([subQ5])]})])],"derivedFrom":makeQuery(id+"F1.opExtrude","CAP_FACE",FACE,{"disambiguationData":[OSD([subQ5,subQ7,subQ8,subQ9,subQ4,subQ3,subQ2,subQ1,subQ6,subQ0,subQ10,subQ11])],"isStart":true})});}
            var sketch = newSketch(context, id + "F16", { "sketchPlane" : qUnion([Q0])});
            skLineSegment(sketch, "E79", {"start": v(-28.67, 90) * mm, "end": v(-15, 108) * mm});
            skLineSegment(sketch, "E80", {"start": v(-15, 108) * mm, "end": v(-15, 119.95) * mm});
            skLineSegment(sketch, "E81", {"start": v(15, 108.05) * mm, "end": v(15, 120) * mm});
            skLineSegment(sketch, "E82", {"start": v(-80, 80) * mm, "end": v(-80, -80) * mm});
            skLineSegment(sketch, "E83", {"start": v(-70, 90) * mm, "end": v(70, 90) * mm});
            skArc(sketch, "E84", {"start": v(-70, 90) * mm, "mid": v(-77.07, 87.07) * mm, "end": v(-80, 80) * mm});
            skLineSegment(sketch, "E85", {"start": v(80, 80) * mm, "end": v(80, -80) * mm});
            skLineSegment(sketch, "E86", {"start": v(-70, -90) * mm, "end": v(70, -90) * mm});
            skArc(sketch, "E87", {"start": v(70, -90) * mm, "mid": v(77.07, -87.07) * mm, "end": v(80, -80) * mm});
            skCircle(sketch, "E88", {"center": v(-60, 67.5) * mm, "radius": 3.38 * mm});
            skArc(sketch, "E89", {"start": v(15, 120) * mm, "mid": v(-0.02, 135) * mm, "end": v(-15, 119.95) * mm});
            skLineSegment(sketch, "E90", {"start": v(15, 108.05) * mm, "end": v(33.05, 90) * mm});
            skCircle(sketch, "E91", {"center": v(0, 120) * mm, "radius": 6 * mm});
            skLineSegment(sketch, "E92", {"start": v(-117.01, 0) * mm, "end": v(96.7, 0) * mm, "construction": true});
            skLineSegment(sketch, "E93.MirrorCS", {"start": v(-28.67, -90) * mm, "end": v(-15, -108) * mm});
            skLineSegment(sketch, "E94.MirrorCS", {"start": v(-15, -108) * mm, "end": v(-15, -119.95) * mm});
            skArc(sketch, "E95.MirrorCS", {"start": v(15, -120) * mm, "mid": v(-0.02, -135) * mm, "end": v(-15, -119.95) * mm});
            skLineSegment(sketch, "E96.MirrorCS", {"start": v(15, -108.05) * mm, "end": v(15, -120) * mm});
            skLineSegment(sketch, "E97.MirrorCS", {"start": v(15, -108.05) * mm, "end": v(33.05, -90) * mm});
            skCircle(sketch, "E98.MirrorC", {"center": v(0, -120) * mm, "radius": 6 * mm});
            skLineSegment(sketch, "E99", {"start": v(0, -120) * mm, "end": v(0, -90) * mm, "construction": true});
            skLineSegment(sketch, "E100", {"start": v(0, 120) * mm, "end": v(0, 90) * mm, "construction": true});
            skSolve(sketch);
        }
        {
            var Q0;
            {var subQ1=sQuery(id+"F16.wireOp",EDGE,"E79");Q0=makeQuery(id+"F16.imprint","IMPRINT",FACE,{"disambiguationData":[TD([[makeQuery(id+"F16.imprint","IMPRINT",EDGE,{"derivedFrom":subQ1}),-1.0]])]});}
            var Q1;
            {var subQ0=sQuery(id+"F16.wireOp",EDGE,"E93.MirrorCS");Q1=makeQuery(id+"F16.imprint","IMPRINT",FACE,{"disambiguationData":[TD([[makeQuery(id+"F16.imprint","IMPRINT",EDGE,{"derivedFrom":subQ0}),1.0]])]});}
            var Q2;
            Q2=makeQuery(id+"F16.imprint","IMPRINT",FACE,{"disambiguationData":[TD([[makeQuery(id+"F16.imprint","IMPRINT",EDGE,{"derivedFrom":sQuery(id+"F16.wireOp",EDGE,"E82")}),-1.0]])]});
            extrude(context, id + "F17", {"entities" : qUnion([Q0, Q1, Q2]), "depth" : 3 * mm});
        }
    });
